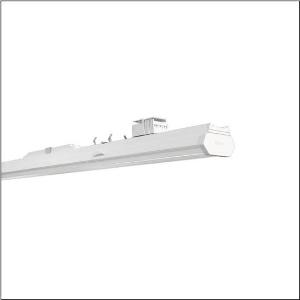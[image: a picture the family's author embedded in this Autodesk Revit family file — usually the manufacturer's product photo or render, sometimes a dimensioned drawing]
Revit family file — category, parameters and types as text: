
# Revit family: licross_r__11_protected_mo_51tp12dn495g_6914
name_source: partatom
category: Lighting Fixtures
units: mm (PartAtom-declared; Revit-internal decimal feet)

## family parameters
Cut with Voids When Loaded = No
Host = Face
Light Source = No
Part Type = Normal
Room Calculation Point = No
Round Connector Dimension = Use Diameter
Shared = No

## types (1)
- --- (1 x LED, 9980 lm, 57.1 W, 4000K)
    Apparent Load = 57 VA
    CIE Flux Codes = 73 92 98 99 100
    Color Rendering = 80
    Color Temperature = 4000K
    Default Elevation = 1800 mm
    Description = Licross® 11 Protected MO, luminaire insert, of sheet steel, galvanised, coil coated, white, length: 1.500mm, width: 90mm, height: 101mm, LED rated luminous flux: 9.980lm, light colour: 840, SDCM (Standard Deviation of Colour Matching)MacAdam ≤ 2 SDCM (initial), control gear: DALI 2, with plug, 5-pole, with phase selection, mains connection: 220..240V, AC, 50/60Hz, rated input power: 57W, internal wiring halogen-free, primary optical cover: cover, of PMMA, light emission: direct distribution, primary light characteristic: symmetric, protection rating (complete): IP64, insulation class (complete): insulation class I (protective earthing), certification: CE, ENEC, VDE, UKCA, protection symbol: D if used in an environment with conductive dust loads with corresponding accessories, impact resistance: IK06, permissible ambient temperature for indoor applications: -25..+35°C, corresponds to IFS (International Featured Standards) requirements for safety and quality in the food industry, reducing of maximum allowable ambient temperature of 5°C with ceiling mounting, LABS conformity tested according to VDMA 24364:2018-05, packaging unit: 1 piece
    Height = 92 mm
    Lamp = 1 x LED
    Lamp Light Flux = 9980 lm
    Lamp Power = 57.1 W
    Lamp count = 1
    Length = 1500 mm
    Luminous efficacy = 175 lm/W
    Manufacturer = Siteco
    ModVariant = No
    Model = 51TP12DN495G
    Mounting Place = Ceiling
    Mounting Type = Pendant
    Number of Poles = 1
    OnlyDefault = Yes
    Power Factor = 1
    Product Name = Licross® 11 Protected MO
    Product group = luminaire insert | ceiling pendant
    ProductGroupID = 901
    Protection Class = Protection class I
    Protection Degree = IP 64
    RLX_Detail_Level = 1
    RLX_Emergency_Light_Flux = 0 lm
    RLX_Emergency_Type = 0
    RLX_Emergency_Type_DB = No
    RlxData = <blob elided: 24585 chars, md5=4d09edbf>
    Socket = socket
    Standby Power = 0 W
    System Light Flux = 9980 lm
    System Power = 57 W
    Type Comments = factory setting: luminous flux: 100 % | dim-lin: 254 | 378 mA
    Type Image = l_1256148.jpg
    URL = http://relux.com
    VarID = @adj_106641
    Voltage = 0 V
    Weight = 0.00 kg
    Width = 88 mm

## geometry (parser evidence)
native form markers: Blend x4, Sweep x8
no freeform markers — native parametric forms only
